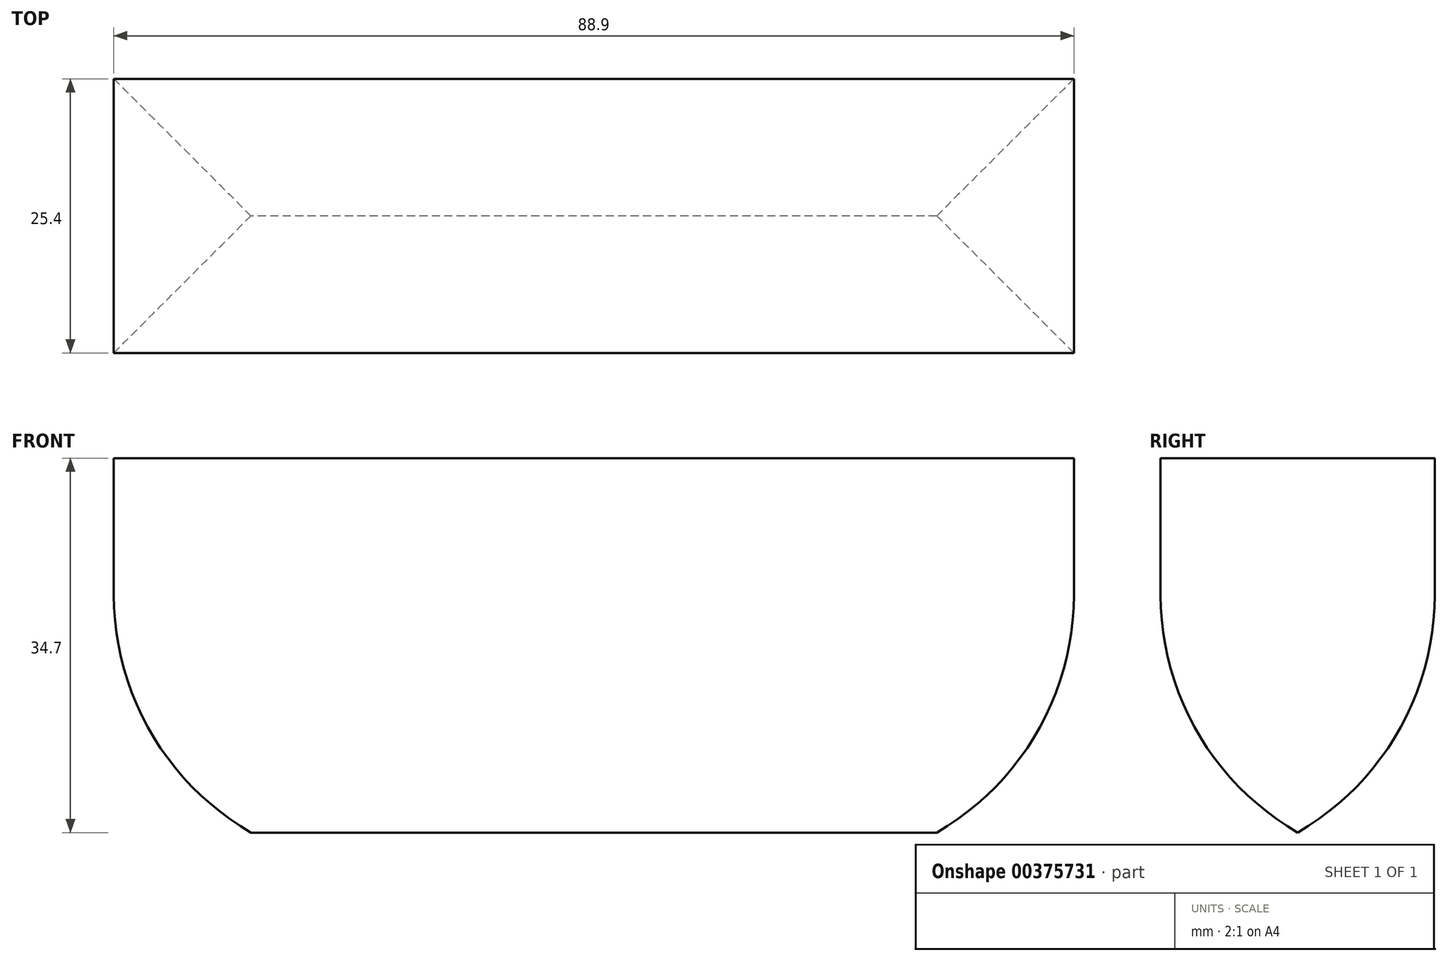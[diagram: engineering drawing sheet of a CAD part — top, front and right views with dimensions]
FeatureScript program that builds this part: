
annotation { "Feature Type Name" : "Feature", "Feature Type Description" : "" }
export const myFeature = defineFeature(function(context is Context, id is Id, definition is map)
    precondition{}
    {
        {
            var Q0;
            Q0=qCreatedBy(makeId("Front.planeOp"),FACE);
            var sketch = newSketch(context, id + "F0", { "sketchPlane" : qUnion([Q0])});
            skLineSegment(sketch, "E0.bottom", {"start": v(44.45, 19.05) * mm, "end": v(-44.45, 19.05) * mm});
            skLineSegment(sketch, "E0.top", {"start": v(44.45, -19.05) * mm, "end": v(-44.45, -19.05) * mm});
            skLineSegment(sketch, "E0.left", {"start": v(44.45, 19.05) * mm, "end": v(44.45, -19.05) * mm});
            skLineSegment(sketch, "E0.right", {"start": v(-44.45, 19.05) * mm, "end": v(-44.45, -19.05) * mm});
            skPoint(sketch, "E0.middle", {"position": v(0, 0) * mm});
            skSolve(sketch);
        }
        {
            var Q0;
            Q0 = qSketchRegion(id + "F0", true);
            extrude(context, id + "F1", {"entities" : qUnion([Q0]), "depth" : 25.4 * mm});
        }
        {
            var Q0;
            Q0=makeQuery(id+"F1.opExtrude","SWEPT_EDGE",EDGE,{"disambiguationData":[OSD([sQuery(id+"F0.wireOp",EDGE,"E0.top"),sQuery(id+"F0.wireOp",EDGE,"E0.left")])]});
            var Q1;
            Q1=makeQuery(id+"F1.opExtrude","SWEPT_EDGE",EDGE,{"disambiguationData":[OSD([sQuery(id+"F0.wireOp",EDGE,"E0.top"),sQuery(id+"F0.wireOp",EDGE,"E0.right")])]});
            var Q2;
            Q2=makeQuery(id+"F1.opExtrude","CAP_EDGE",EDGE,{"disambiguationData":[OSD([sQuery(id+"F0.wireOp",EDGE,"E0.top")])],"isStart":false});
            var Q3;
            Q3=makeQuery(id+"F1.opExtrude","CAP_EDGE",EDGE,{"disambiguationData":[OSD([sQuery(id+"F0.wireOp",EDGE,"E0.top")])],"isStart":true});
            fillet(context, id + "F2", {"entities" : qUnion([Q0, Q1, Q2, Q3]), "radius" : 25.4 * mm, "tangentPropagation" : true, "allowEdgeOverflow" : false});
        }
    });
